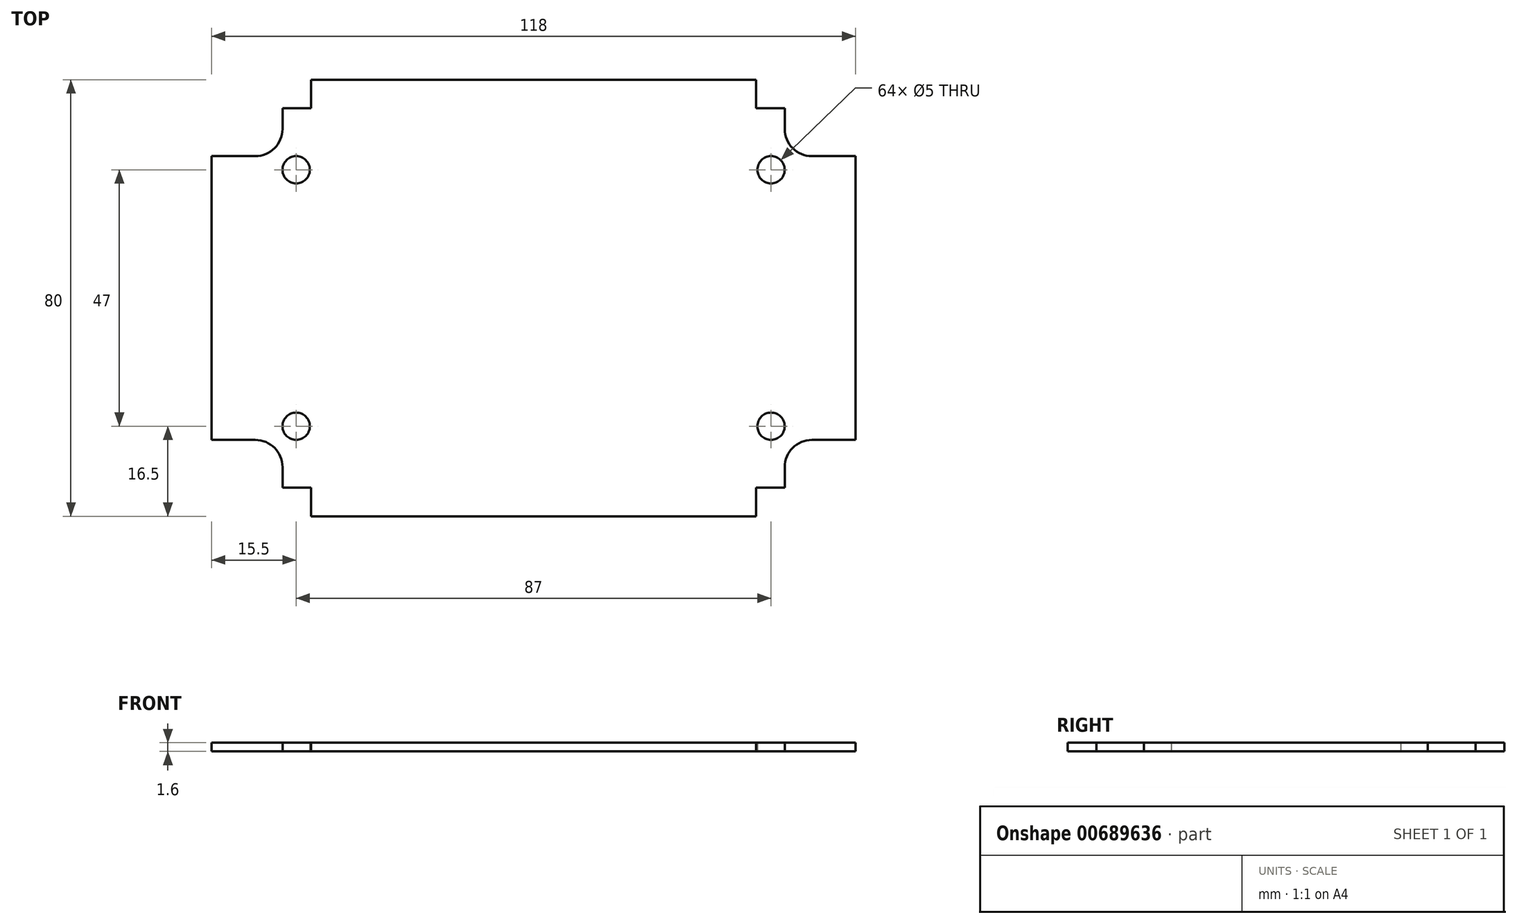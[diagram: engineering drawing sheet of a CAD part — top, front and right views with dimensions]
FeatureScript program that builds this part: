
annotation { "Feature Type Name" : "Feature", "Feature Type Description" : "" }
export const myFeature = defineFeature(function(context is Context, id is Id, definition is map)
    precondition{}
    {
        {
            var Q0;
            Q0=qCreatedBy(makeId("Top.planeOp"),FACE);
            var sketch = newSketch(context, id + "F0", { "sketchPlane" : qUnion([Q0])});
            skArc(sketch, "E0", {"start": v(11.5, 68.5) * mm, "mid": v(15.04, 69.96) * mm, "end": v(16.5, 73.5) * mm});
            skCircle(sketch, "E1", {"center": v(19, 66) * mm, "radius": 2.5 * mm});
            skCircle(sketch, "E2", {"center": v(106, 66) * mm, "radius": 2.5 * mm});
            skArc(sketch, "E3", {"start": v(108.5, 73.5) * mm, "mid": v(109.96, 69.96) * mm, "end": v(113.5, 68.5) * mm});
            skCircle(sketch, "E4", {"center": v(106, 19) * mm, "radius": 2.5 * mm});
            skArc(sketch, "E5", {"start": v(113.5, 16.5) * mm, "mid": v(109.96, 15.04) * mm, "end": v(108.5, 11.5) * mm});
            skCircle(sketch, "E6", {"center": v(19, 19) * mm, "radius": 2.5 * mm});
            skLineSegment(sketch, "E7", {"start": v(16.5, 73.5) * mm, "end": v(16.5, 77.25) * mm});
            skLineSegment(sketch, "E8", {"start": v(113.5, 68.5) * mm, "end": v(121.5, 68.5) * mm});
            skLineSegment(sketch, "E9", {"start": v(108.5, 73.5) * mm, "end": v(108.5, 77.25) * mm});
            skLineSegment(sketch, "E10", {"start": v(108.5, 11.5) * mm, "end": v(108.5, 7.75) * mm});
            skLineSegment(sketch, "E11", {"start": v(113.5, 16.5) * mm, "end": v(121.5, 16.5) * mm});
            skLineSegment(sketch, "E12", {"start": v(11.5, 16.5) * mm, "end": v(3.5, 16.5) * mm});
            skLineSegment(sketch, "E13", {"start": v(16.5, 11.5) * mm, "end": v(16.5, 7.75) * mm});
            skArc(sketch, "E14.trimOffspring", {"start": v(16.5, 11.5) * mm, "mid": v(15.04, 15.04) * mm, "end": v(11.5, 16.5) * mm});
            skLineSegment(sketch, "E15", {"start": v(3.5, 68.5) * mm, "end": v(11.5, 68.5) * mm});
            skLineSegment(sketch, "E16.0", {"start": v(3.5, 16.5) * mm, "end": v(3.5, 68.5) * mm});
            skLineSegment(sketch, "E17.0", {"start": v(121.5, 16.5) * mm, "end": v(121.5, 68.5) * mm});
            skLineSegment(sketch, "E18.0", {"start": v(21.75, 82.5) * mm, "end": v(103.25, 82.5) * mm});
            skLineSegment(sketch, "E19.0", {"start": v(21.75, 2.5) * mm, "end": v(103.25, 2.5) * mm});
            skLineSegment(sketch, "E20.0", {"start": v(21.75, 77.25) * mm, "end": v(21.75, 81) * mm});
            skLineSegment(sketch, "E21.0", {"start": v(103.25, 77.25) * mm, "end": v(103.25, 81) * mm});
            skLineSegment(sketch, "E22", {"start": v(16.5, 77.25) * mm, "end": v(21.75, 77.25) * mm});
            skLineSegment(sketch, "E23", {"start": v(103.25, 81) * mm, "end": v(103.25, 82.5) * mm});
            skLineSegment(sketch, "E24", {"start": v(21.75, 81) * mm, "end": v(21.75, 82.5) * mm});
            skLineSegment(sketch, "E25.trimOffspring", {"start": v(103.25, 77.25) * mm, "end": v(108.5, 77.25) * mm});
            skLineSegment(sketch, "E26", {"start": v(16.5, 7.75) * mm, "end": v(21.75, 7.75) * mm});
            skLineSegment(sketch, "E27.0", {"start": v(21.75, 7.75) * mm, "end": v(21.75, 4) * mm});
            skLineSegment(sketch, "E28.0", {"start": v(103.25, 7.75) * mm, "end": v(103.25, 4) * mm});
            skLineSegment(sketch, "E29", {"start": v(21.75, 4) * mm, "end": v(21.75, 2.5) * mm});
            skLineSegment(sketch, "E30", {"start": v(103.25, 4) * mm, "end": v(103.25, 2.5) * mm});
            skLineSegment(sketch, "E31.trimOffspring", {"start": v(103.25, 7.75) * mm, "end": v(108.5, 7.75) * mm});
            skSolve(sketch);
        }
        {
            var Q0;
            Q0 = qSketchRegion(id + "F0", true);
            extrude(context, id + "F1", {"entities" : qUnion([Q0]), "depth" : 1.6 * mm, "offsetDistance" : 25.4 * mm});
        }
    });
